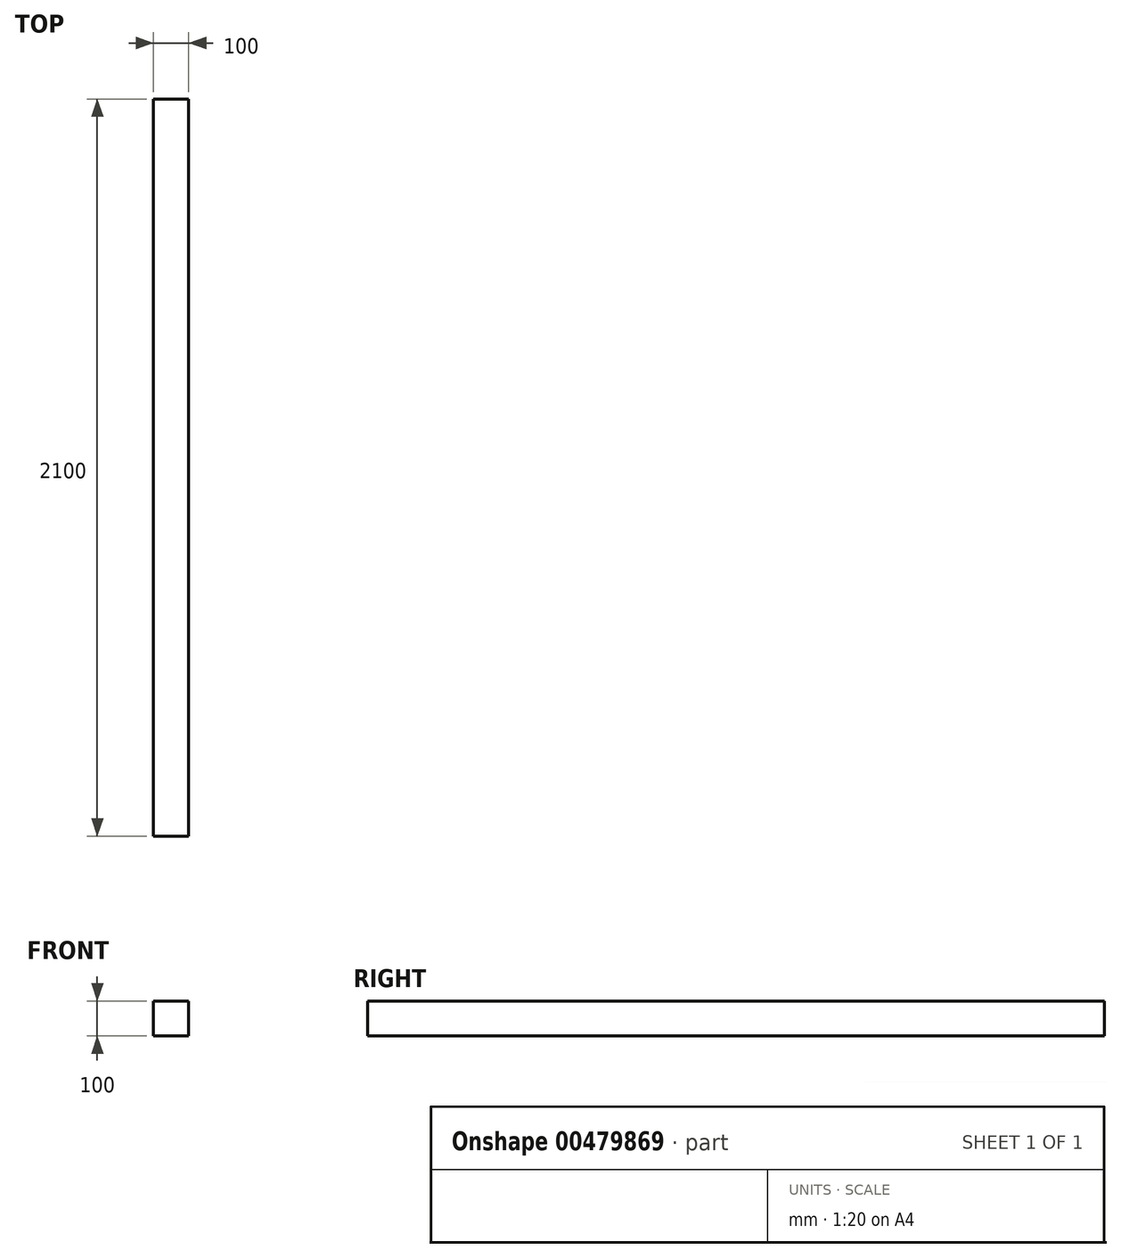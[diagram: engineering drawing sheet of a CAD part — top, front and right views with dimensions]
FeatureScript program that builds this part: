
annotation { "Feature Type Name" : "Feature", "Feature Type Description" : "" }
export const myFeature = defineFeature(function(context is Context, id is Id, definition is map)
    precondition{}
    {
        {
            var Q0;
            Q0=qCreatedBy(makeId("Right.planeOp"),FACE);
            var sketch = newSketch(context, id + "F0", { "sketchPlane" : qUnion([Q0])});
            skLineSegment(sketch, "E0", {"start": v(0, 0) * mm, "end": v(0, -100) * mm});
            skLineSegment(sketch, "E1", {"start": v(0, -100) * mm, "end": v(-2100, -100) * mm});
            skLineSegment(sketch, "E2", {"start": v(-2100, -100) * mm, "end": v(-2100, 0) * mm});
            skLineSegment(sketch, "E3", {"start": v(-2100, 0) * mm, "end": v(0, 0) * mm});
            skSolve(sketch);
        }
        {
            var Q0;
            Q0=makeQuery(id+"F0.imprint","IMPRINT",FACE,{"disambiguationData":[TD([[makeQuery(id+"F0.imprint","IMPRINT",EDGE,{"derivedFrom":sQuery(id+"F0.wireOp",EDGE,"E0")}),-1.0]])]});
            extrude(context, id + "F1", {"entities" : qUnion([Q0]), "depth" : 100 * mm});
        }
    });
